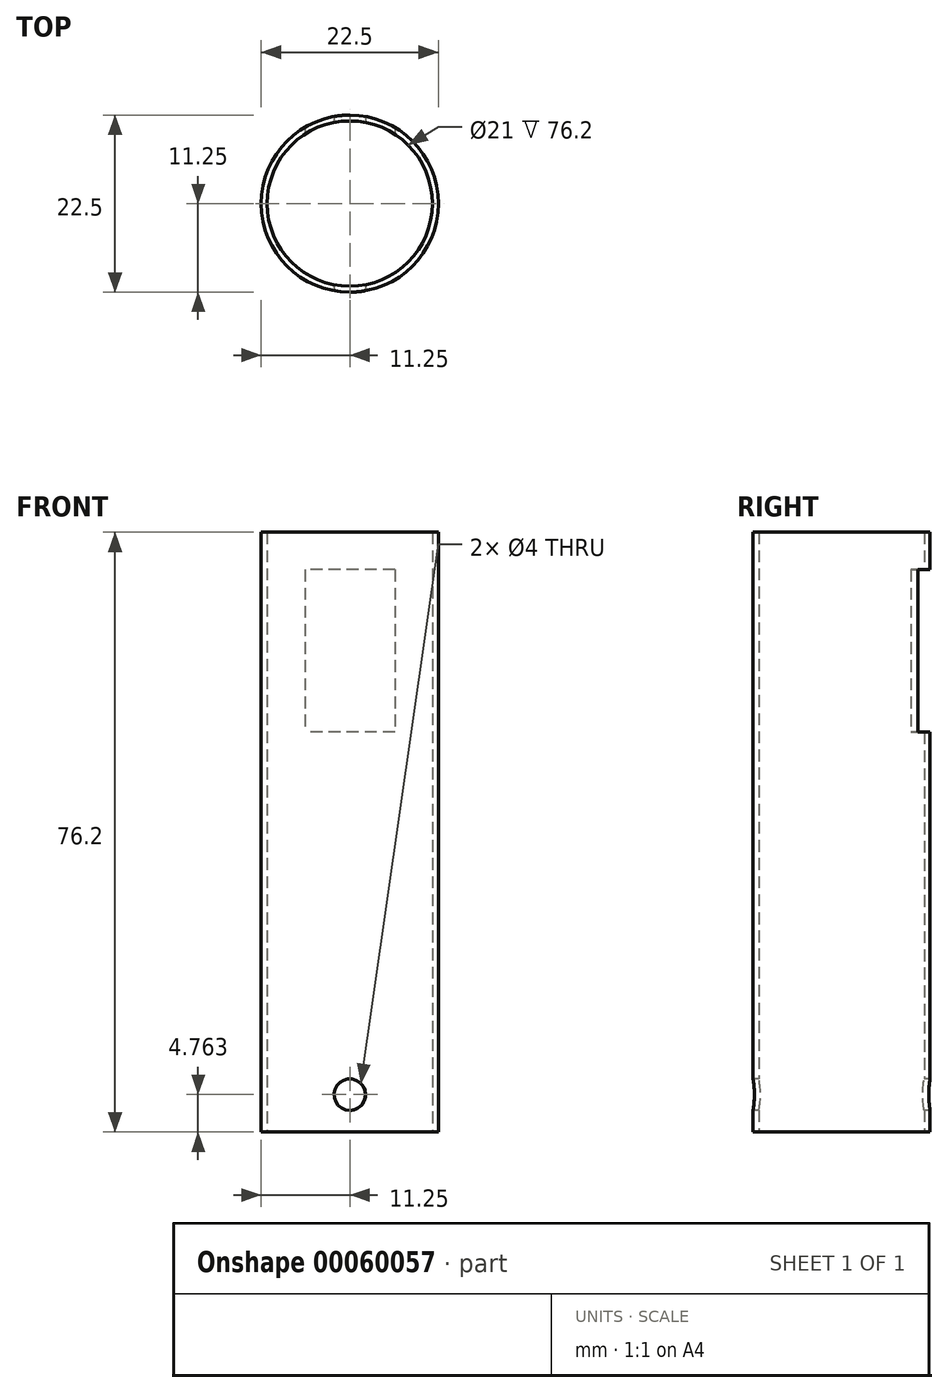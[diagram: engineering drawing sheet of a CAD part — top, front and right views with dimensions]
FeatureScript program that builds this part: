
annotation { "Feature Type Name" : "Feature", "Feature Type Description" : "" }
export const myFeature = defineFeature(function(context is Context, id is Id, definition is map)
    precondition{}
    {
        {
            var Q0;
            Q0=qCreatedBy(makeId("Top.planeOp"),FACE);
            var sketch = newSketch(context, id + "F0", { "sketchPlane" : qUnion([Q0])});
            skCircle(sketch, "E0", {"center": v(0, 0) * mm, "radius": 10.5 * mm});
            skCircle(sketch, "E1", {"center": v(0, 0) * mm, "radius": 11.25 * mm});
            skSolve(sketch);
        }
        {
            var Q0;
            Q0 = qSketchRegion(id + "F0", true);
            extrude(context, id + "F1", {"entities" : qUnion([Q0]), "depth" : 76.2 * mm});
        }
        {
            var Q0;
            Q0=qCreatedBy(makeId("Front.planeOp"),FACE);
            var sketch = newSketch(context, id + "F2", { "sketchPlane" : qUnion([Q0])});
            skLineSegment(sketch, "E2.rect.bottom", {"start": v(5.71, 50.8) * mm, "end": v(-5.71, 50.8) * mm});
            skLineSegment(sketch, "E2.rect.top", {"start": v(5.72, 71.44) * mm, "end": v(-5.71, 71.44) * mm});
            skLineSegment(sketch, "E2.rect.left", {"start": v(5.72, 50.8) * mm, "end": v(5.72, 71.44) * mm});
            skLineSegment(sketch, "E2.rect.right", {"start": v(-5.71, 50.8) * mm, "end": v(-5.71, 71.44) * mm});
            skPoint(sketch, "E2.rect.middle", {"position": v(0, 61.12) * mm});
            skSolve(sketch);
        }
        {
            var Q0;
            Q0 = qSketchRegion(id + "F2", true);
            extrude(context, id + "F3", {"entities" : qUnion([Q0]), "operationType" : NewBodyOperationType.REMOVE, "oppositeDirection" : true, "depth" : 25.4 * mm});
        }
        {
            var Q0;
            Q0=qCreatedBy(makeId("Front.planeOp"),FACE);
            var sketch = newSketch(context, id + "F4", { "sketchPlane" : qUnion([Q0])});
            skLineSegment(sketch, "E3", {"start": v(0, 0) * mm, "end": v(0, 4.76) * mm});
            skCircle(sketch, "E4", {"center": v(0, 4.76) * mm, "radius": 2 * mm});
            skSolve(sketch);
        }
        {
            var Q0;
            Q0 = qSketchRegion(id + "F4", true);
            extrude(context, id + "F5", {"entities" : qUnion([Q0]), "operationType" : NewBodyOperationType.REMOVE, "oppositeDirection" : true, "depth" : 25.4 * mm, "hasSecondDirection" : true, "secondDirectionOppositeDirection" : false, "secondDirectionDepth" : 25.4 * mm});
        }
    });
